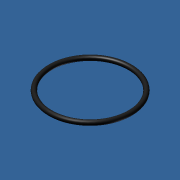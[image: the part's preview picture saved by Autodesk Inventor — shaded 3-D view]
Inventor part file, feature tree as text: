
AUTODESK INVENTOR PART (.ipt)
format: ipt  version: unknown  size: 184,320 bytes
history: native  units: in
note: dims shown in document units (in); Inventor stores cm internally (conversion verified against a paired STEP export)
features: revolve x1, sketch x1
ambient origin geometry x8: Origin, YZ Plane, XZ Plane, XY Plane, X Axis, Y Axis, Z Axis, Center Point
bodies: Solid1 (feature_tree)
feature tree (2):
  revolve  "Revolution1"  [1 undecoded]
  sketch  "Sketch1"  dims[d2=0.075in d3=0.6625in d4=90.0deg]
note: 1 required parameter value undecoded (feature->parameter linkage not recoverable at this tier; creation-order binding heuristic only, values carry confidence <= 0.55)
